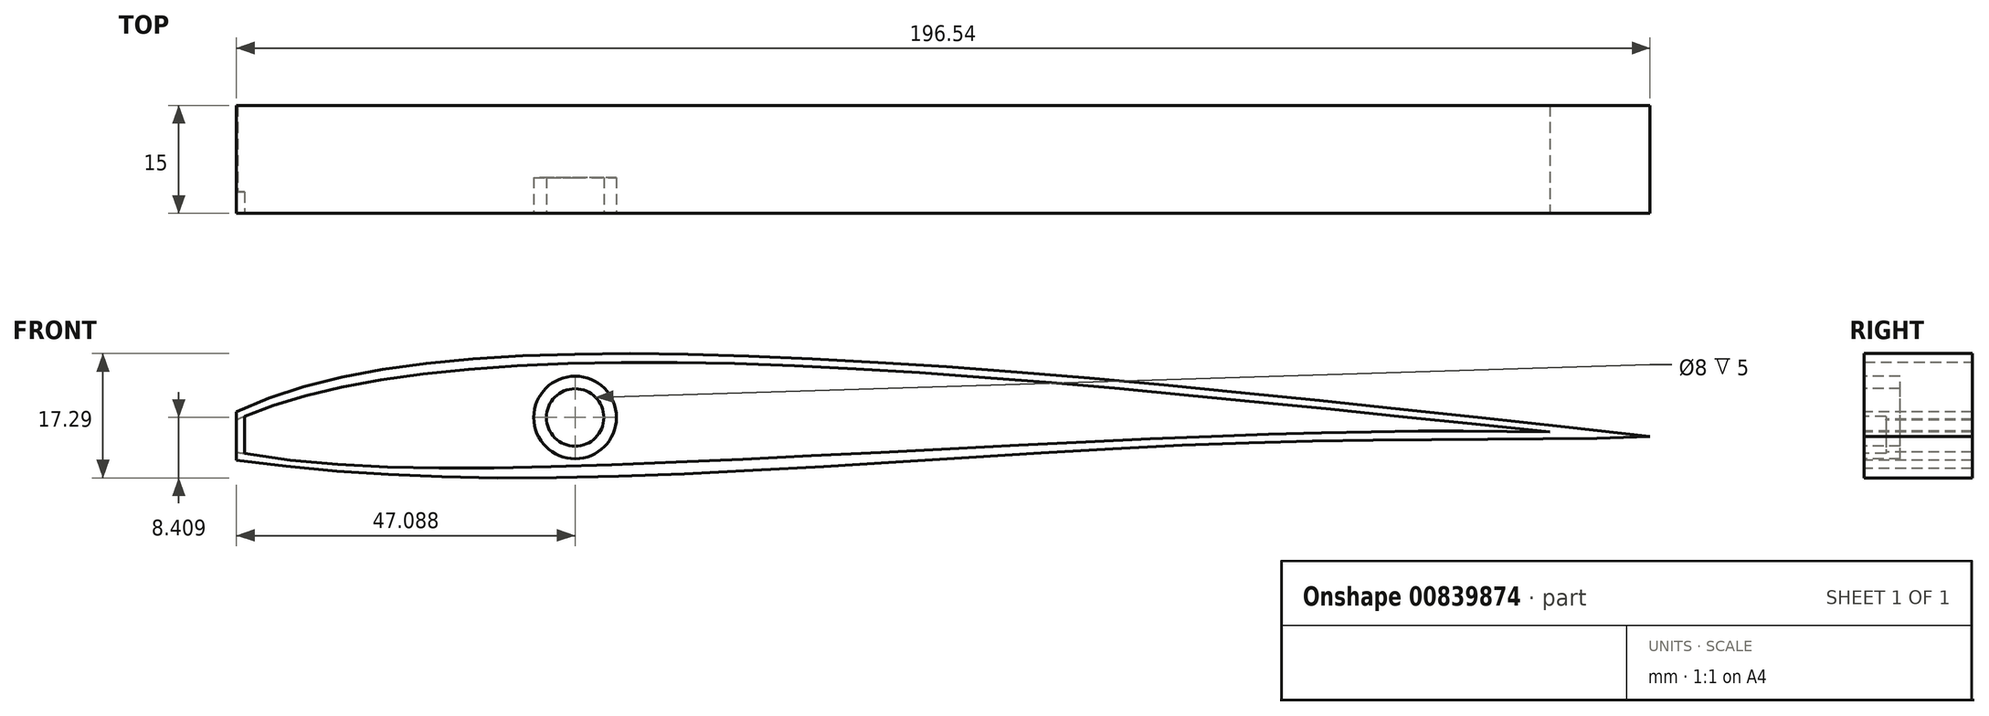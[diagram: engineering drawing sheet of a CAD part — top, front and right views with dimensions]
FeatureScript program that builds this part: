
annotation { "Feature Type Name" : "Feature", "Feature Type Description" : "" }
export const myFeature = defineFeature(function(context is Context, id is Id, definition is map)
    precondition{}
    {
        {
            var Q0;
            Q0=qCreatedBy(makeId("Front.planeOp"),FACE);
            var sketch = newSketch(context, id + "F0", { "sketchPlane" : qUnion([Q0])});
            skPoint(sketch, "E0.middle", {"position": v(0, 0) * mm});
            skFitSpline(sketch, "E1", {"points": [v(-96.98, -0.81) * mm, v(-45.24, 7.5) * mm, v(100, -4.05) * mm], "startDerivative": vector(97.58, 47.67) * mm, "endDerivative": vector(275.05, -31.29) * mm});
            skFitSpline(sketch, "E2", {"points": [v(-96.54, -7.34) * mm, v(-44.56, -9.6) * mm, v(41.7, -4.97) * mm, v(100, -4.05) * mm], "startDerivative": vector(159.07, -20.98) * mm, "endDerivative": vector(169.88, 6) * mm});
            skFitSpline(sketch, "E3", {"points": [v(-96.34, -1.64) * mm, v(-45.34, 6.27) * mm, v(86.1, -3.38) * mm], "startDerivative": vector(82.57, 38.4) * mm, "endDerivative": vector(239.73, -24.74) * mm});
            skFitSpline(sketch, "E4", {"points": [v(-97.38, -6.05) * mm, v(-44.49, -7.96) * mm, v(41.39, -3.9) * mm, v(86.1, -3.38) * mm], "startDerivative": vector(144.05, -26.77) * mm, "endDerivative": vector(139.27, -2.3) * mm});
            skLineSegment(sketch, "E5", {"start": v(-95.4, -1.21) * mm, "end": v(-95.4, -6.4) * mm});
            skLineSegment(sketch, "E6", {"start": v(-96.54, -0.6) * mm, "end": v(-96.54, -7.34) * mm});
            skFitSpline(sketch, "E7.trimOffspring", {"points": [v(-97.38, -6.05) * mm, v(-99.95, -4.56) * mm, v(-96.34, -1.64) * mm], "startDerivative": vector(-8.62, 1.03) * mm, "endDerivative": vector(10.24, 4.38) * mm});
            skPoint(sketch, "E8.trimOffspring.center.orphan", {"position": v(-96.34, -4.05) * mm});
            skPoint(sketch, "E9.1.internal.orphan", {"position": v(-101.41, -5) * mm});
            skPoint(sketch, "E10.start.orphan", {"position": v(-99.95, -4.05) * mm});
            skCircle(sketch, "E11", {"center": v(-49.45, -1.37) * mm, "radius": 4 * mm});
            skCircle(sketch, "E12", {"center": v(33.78, -1.03) * mm, "radius": 2.5 * mm});
            skLineSegment(sketch, "E13", {"start": v(-56.42, 4.45) * mm, "end": v(-56.42, -7.2) * mm});
            skLineSegment(sketch, "E14", {"start": v(-94.27, -1.68) * mm, "end": v(-94.27, -5.45) * mm});
            skFitSpline(sketch, "E15", {"points": [v(-94.27, -1.68) * mm, v(-75.44, 3) * mm, v(-56.42, 4.45) * mm], "startDerivative": vector(37.23, 13.11) * mm, "endDerivative": vector(37.06, -0.15) * mm});
            skFitSpline(sketch, "E16", {"points": [v(-56.42, -7.2) * mm, v(-75.86, -7.2) * mm, v(-94.27, -5.45) * mm], "startDerivative": vector(-38.67, -0.9) * mm, "endDerivative": vector(-37.01, 4.45) * mm});
            skLineSegment(sketch, "E17", {"start": v(-90.05, -0.3) * mm, "end": v(-86.02, -6.4) * mm});
            skLineSegment(sketch, "E18", {"start": v(-83.6, -6.64) * mm, "end": v(-75.44, 3) * mm});
            skLineSegment(sketch, "E19", {"start": v(-73.9, 3.22) * mm, "end": v(-66.47, -7.38) * mm});
            skLineSegment(sketch, "E20", {"start": v(-62.95, -7.36) * mm, "end": v(-56.42, 4.45) * mm});
            skLineSegment(sketch, "E21", {"start": v(-72.03, 3.47) * mm, "end": v(-64.9, -6.69) * mm});
            skLineSegment(sketch, "E22", {"start": v(-64.9, -6.69) * mm, "end": v(-58.76, 4.43) * mm});
            skLineSegment(sketch, "E23", {"start": v(-88.04, 0.29) * mm, "end": v(-84.32, -5.34) * mm});
            skLineSegment(sketch, "E24", {"start": v(-84.32, -5.34) * mm, "end": v(-77.56, 2.64) * mm});
            skFitSpline(sketch, "E25.trimOffspring", {"points": [v(-94.27, -1.68) * mm, v(-75.44, 3) * mm, v(-56.42, 4.45) * mm], "startDerivative": vector(37.23, 13.11) * mm, "endDerivative": vector(37.06, -0.15) * mm});
            skLineSegment(sketch, "E26", {"start": v(-39.23, 5.3) * mm, "end": v(-39.23, -6.51) * mm});
            skLineSegment(sketch, "E27", {"start": v(28.07, 1.28) * mm, "end": v(28.07, -3.67) * mm});
            skFitSpline(sketch, "E28", {"points": [v(-39.23, 5.3) * mm, v(-6.24, 3.91) * mm, v(28.07, 1.28) * mm], "startDerivative": vector(66.36, -2.2) * mm, "endDerivative": vector(68.23, -5.84) * mm});
            skFitSpline(sketch, "E29", {"points": [v(28.07, -3.67) * mm, v(-6.7, -5.32) * mm, v(-39.23, -6.51) * mm], "startDerivative": vector(-68.96, -3.46) * mm, "endDerivative": vector(-65.62, -2.21) * mm});
            skLineSegment(sketch, "E30", {"start": v(-39.23, -6.51) * mm, "end": v(-29.4, 4.97) * mm});
            skLineSegment(sketch, "E31", {"start": v(-27.29, 4.89) * mm, "end": v(-21.61, -5.9) * mm});
            skLineSegment(sketch, "E32", {"start": v(-21.48, -5.9) * mm, "end": v(-15.64, 4.4) * mm});
            skLineSegment(sketch, "E33", {"start": v(-36.65, -6.42) * mm, "end": v(-28.28, 3.34) * mm});
            skLineSegment(sketch, "E34", {"start": v(-28.28, 3.34) * mm, "end": v(-23.39, -5.97) * mm});
            skLineSegment(sketch, "E35", {"start": v(-19.55, -5.83) * mm, "end": v(-14.5, 3.08) * mm});
            skLineSegment(sketch, "E36", {"start": v(-14.5, 3.08) * mm, "end": v(-10, -5.46) * mm});
            skLineSegment(sketch, "E37", {"start": v(-8.67, -5.4) * mm, "end": v(-13.79, 4.32) * mm});
            skLineSegment(sketch, "E38", {"start": v(-8.67, -5.4) * mm, "end": v(-1.68, 3.63) * mm});
            skLineSegment(sketch, "E39", {"start": v(0, 3.51) * mm, "end": v(6.1, -4.75) * mm});
            skLineSegment(sketch, "E40", {"start": v(-6.6, -5.32) * mm, "end": v(-0.65, 2.36) * mm});
            skLineSegment(sketch, "E41", {"start": v(-0.65, 2.36) * mm, "end": v(4.65, -4.82) * mm});
            skLineSegment(sketch, "E42", {"start": v(6.1, -4.75) * mm, "end": v(10.79, 2.72) * mm});
            skLineSegment(sketch, "E43", {"start": v(13.16, 2.53) * mm, "end": v(16.11, -4.27) * mm});
            skLineSegment(sketch, "E44", {"start": v(16.11, -4.27) * mm, "end": v(20.3, 1.94) * mm});
            skLineSegment(sketch, "E45", {"start": v(23.71, 1.65) * mm, "end": v(28.07, -3.67) * mm});
            skLineSegment(sketch, "E46", {"start": v(8, -4.66) * mm, "end": v(11.98, 1.67) * mm});
            skLineSegment(sketch, "E47", {"start": v(11.98, 1.67) * mm, "end": v(14.6, -4.34) * mm});
            skLineSegment(sketch, "E48", {"start": v(18.33, -4.16) * mm, "end": v(22.07, 1.37) * mm});
            skLineSegment(sketch, "E49", {"start": v(22.07, 1.37) * mm, "end": v(26.27, -3.76) * mm});
            skCircle(sketch, "E50", {"center": v(-49.45, -1.37) * mm, "radius": 5.75 * mm});
            skSolve(sketch);
        }
        {
            var Q0;
            Q0=makeQuery(id+"F0.imprint","IMPRINT",FACE,{"disambiguationData":[TD([[makeQuery(id+"F0.imprint","IMPRINT",EDGE,{"derivedFrom":sQuery(id+"F0.wireOp",EDGE,"E3")}),-1.0]])]});
            extrude(context, id + "F1", {"entities" : qUnion([Q0]), "oppositeDirection" : true, "depth" : 3 * mm, "offsetDistance" : 25 * mm});
        }
        {
            var Q0;
            {var subQ1=sQuery(id+"F0.wireOp",EDGE,"E1");Q0=makeQuery(id+"F0.imprint","IMPRINT",FACE,{"disambiguationData":[TD([[makeQuery(id+"F0.imprint","IMPRINT",EDGE,{"derivedFrom":subQ1}),-1.0]])]});}
            extrude(context, id + "F2", {"entities" : qUnion([Q0]), "operationType" : NewBodyOperationType.ADD, "oppositeDirection" : true, "depth" : 15 * mm, "offsetDistance" : 25 * mm});
        }
        {
            var Q0;
            Q0=makeQuery(id+"F0.imprint","IMPRINT",FACE,{"disambiguationData":[TD([[makeQuery(id+"F0.imprint","IMPRINT",EDGE,{"derivedFrom":sQuery(id+"F0.wireOp",EDGE,"E11")}),-1.0]])]});
            extrude(context, id + "F3", {"entities" : qUnion([Q0]), "oppositeDirection" : true, "depth" : 5 * mm, "offsetDistance" : 25 * mm});
        }
    });
